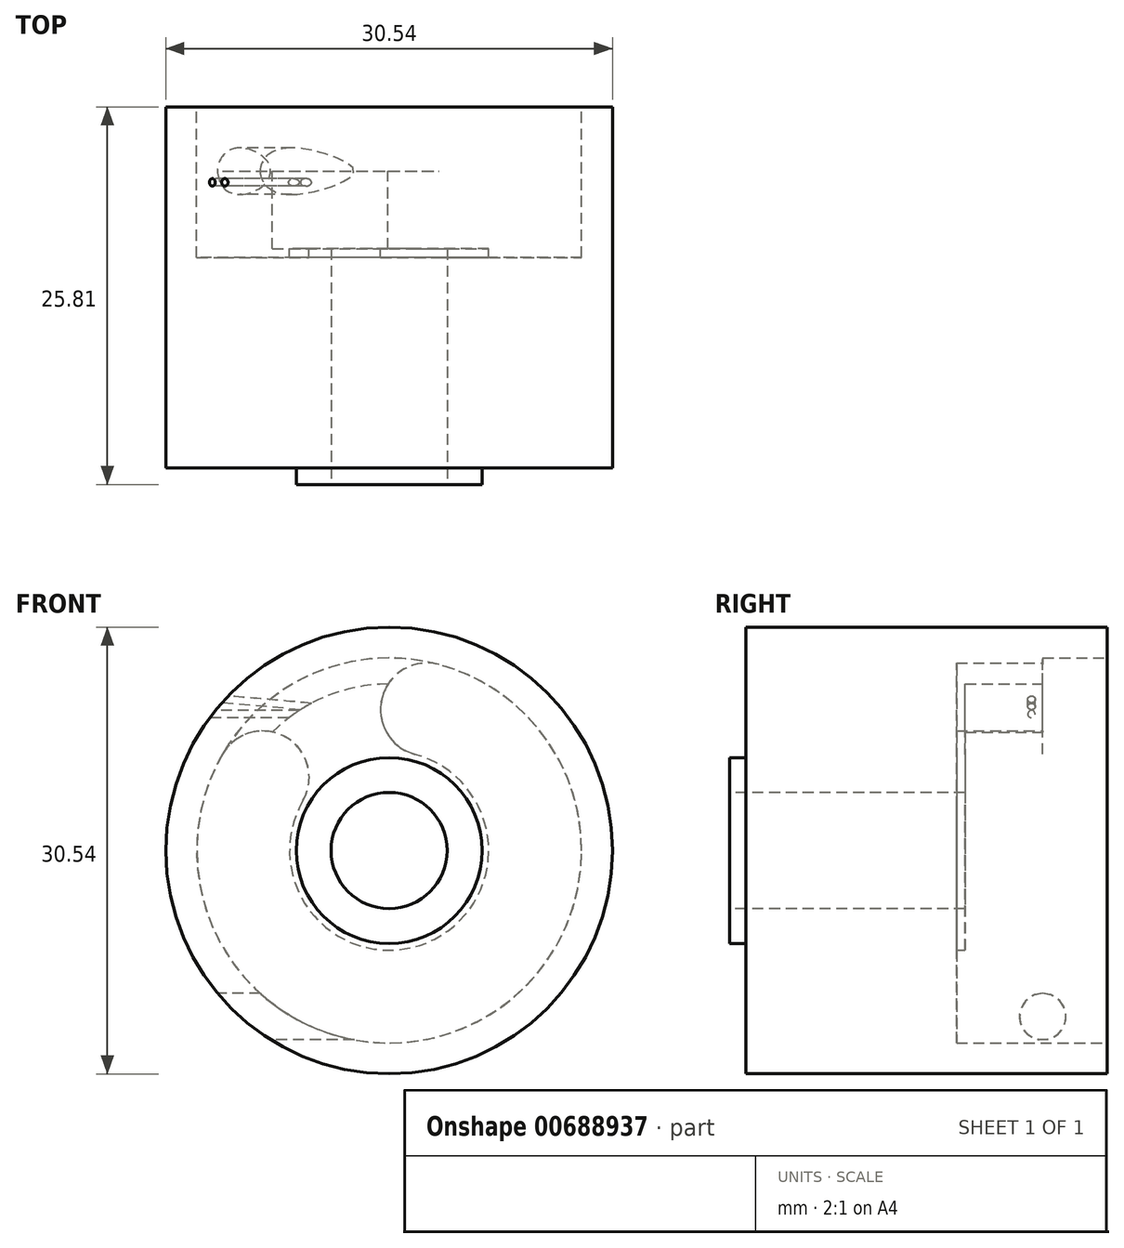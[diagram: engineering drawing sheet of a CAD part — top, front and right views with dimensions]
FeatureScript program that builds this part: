
annotation { "Feature Type Name" : "Feature", "Feature Type Description" : "" }
export const myFeature = defineFeature(function(context is Context, id is Id, definition is map)
    precondition{}
    {
        {
            var Q0;
            Q0=qCreatedBy(makeId("Front.planeOp"),FACE);
            var sketch = newSketch(context, id + "F0", { "sketchPlane" : qUnion([Q0])});
            skCircle(sketch, "E0", {"center": v(0, 0) * mm, "radius": 3.97 * mm});
            skCircle(sketch, "E1", {"center": v(0, 0) * mm, "radius": 15.27 * mm});
            skSolve(sketch);
        }
        {
            var Q0;
            Q0=qSketchRegion(id+"F0",true);
            extrude(context, id + "F1", {"entities" : qUnion([Q0]), "oppositeDirection" : true, "depth" : 24.7 * mm});
        }
        {
            var Q0;
            Q0=qCreatedBy(makeId("Front.planeOp"),FACE);
            var sketch = newSketch(context, id + "F2", { "sketchPlane" : qUnion([Q0])});
            skCircle(sketch, "E2", {"center": v(0, 0) * mm, "radius": 3.97 * mm});
            skCircle(sketch, "E3", {"center": v(0, 0) * mm, "radius": 6.35 * mm});
            skSolve(sketch);
        }
        {
            var Q0;
            Q0=qSketchRegion(id+"F2",true);
            extrude(context, id + "F3", {"entities" : qUnion([Q0]), "operationType" : NewBodyOperationType.ADD, "depth" : 1.12 * mm});
        }
        {
            var Q0;
            Q0=makeQuery(id+"F1.opExtrude","CAP_FACE",FACE,{"disambiguationData":[OSD([sQuery(id+"F0.wireOp",EDGE,"E0"),sQuery(id+"F0.wireOp",EDGE,"E1")])],"isStart":false});
            var sketch = newSketch(context, id + "F4", { "sketchPlane" : qUnion([Q0])});
            skCircle(sketch, "E4", {"center": v(0, 0) * mm, "radius": 13.16 * mm});
            skSolve(sketch);
        }
        {
            var Q0;
            Q0=qSketchRegion(id+"F4",true);
            extrude(context, id + "F5", {"entities" : qUnion([Q0]), "operationType" : NewBodyOperationType.REMOVE, "oppositeDirection" : true, "depth" : 4.4 * mm});
        }
        {
            var Q0;
            Q0=makeQuery(id+"F5.boolean.opBoolean","COPY",FACE,{"derivedFrom":makeQuery(id+"F5.opExtrude","CAP_FACE",FACE,{"disambiguationData":[OSD([sQuery(id+"F4.wireOp",EDGE,"E4")])],"isStart":false})});
            var sketch = newSketch(context, id + "F6", { "sketchPlane" : qUnion([Q0])});
            skCircle(sketch, "E5", {"center": v(0, 0) * mm, "radius": 9.98 * mm, "construction": true});
            skCircle(sketch, "E6", {"center": v(-2.58, 9.64) * mm, "radius": 3.18 * mm});
            skCircle(sketch, "E7", {"center": v(8.64, 5) * mm, "radius": 3.18 * mm});
            skArc(sketch, "E8", {"start": v(-3.4, 12.7) * mm, "mid": v(-5.04, -12.16) * mm, "end": v(11.4, 6.58) * mm});
            skArc(sketch, "E9", {"start": v(-1.76, 6.58) * mm, "mid": v(-2.6, -6.29) * mm, "end": v(5.9, 3.4) * mm});
            skLineSegment(sketch, "E10", {"start": v(0, 0) * mm, "end": v(0, 22.93) * mm, "construction": true});
            skLineSegment(sketch, "E11", {"start": v(0, 0) * mm, "end": v(-2.58, 9.64) * mm, "construction": true});
            skLineSegment(sketch, "E12", {"start": v(0, 0) * mm, "end": v(8.64, 5) * mm, "construction": true});
            skSolve(sketch);
        }
        {
            var Q0;
            Q0=qSketchRegion(id+"F6",true);
            extrude(context, id + "F7", {"entities" : qUnion([Q0]), "operationType" : NewBodyOperationType.REMOVE, "oppositeDirection" : true, "depth" : 5.9 * mm});
        }
        {
            var Q0;
            Q0=makeQuery(id+"F5.boolean.opBoolean","COPY",FACE,{"derivedFrom":makeQuery(id+"F5.opExtrude","CAP_FACE",FACE,{"disambiguationData":[OSD([sQuery(id+"F4.wireOp",EDGE,"E4")])],"isStart":false})});
            var sketch = newSketch(context, id + "F8", { "sketchPlane" : qUnion([Q0])});
            skCircle(sketch, "E13", {"center": v(0, 0) * mm, "radius": 11.38 * mm});
            skSolve(sketch);
        }
        {
            var Q0;
            Q0=qSketchRegion(id+"F8",true);
            extrude(context, id + "F9", {"entities" : qUnion([Q0]), "operationType" : NewBodyOperationType.REMOVE, "oppositeDirection" : true, "depth" : 5.3 * mm});
        }
        {
            var Q0;
            Q0=qCreatedBy(makeId("Right.planeOp"),FACE);
            cPlane(context, id + "F10", {"entities" : qUnion([Q0]), "cplaneType" : CPlaneType.OFFSET, "offset" : 15.27 * mm, "oppositeDirection" : true, "width" : 152.4 * mm, "height" : 152.4 * mm});
        }
        {
            var Q0;
            Q0=qCreatedBy(id+"F10.planeOp",FACE);
            var sketch = newSketch(context, id + "F11", { "sketchPlane" : qUnion([Q0])});
            skCircle(sketch, "E14", {"center": v(19.53, 10.87) * mm, "radius": 0.36 * mm, "construction": true});
            skCircle(sketch, "E15", {"center": v(20.3, -11.35) * mm, "radius": 1.59 * mm});
            skCircle(sketch, "E16", {"center": v(19.53, 9.32) * mm, "radius": 0.25 * mm});
            skSolve(sketch);
        }
        {
            var Q0;
            Q0=qSketchRegion(id+"F11",true);
            extrude(context, id + "F12", {"entities" : qUnion([Q0]), "operationType" : NewBodyOperationType.REMOVE, "depth" : 15.27 * mm, "offsetDistance" : 25.4 * mm});
        }
        {
            var Q0;
            Q0=makeQuery(id+"F1.opExtrude","CAP_FACE",FACE,{"disambiguationData":[OSD([sQuery(id+"F0.wireOp",EDGE,"E0"),sQuery(id+"F0.wireOp",EDGE,"E1")])],"isStart":false});
            var sketch = newSketch(context, id + "F13", { "sketchPlane" : qUnion([Q0])});
            skLineSegment(sketch, "E17", {"start": v(0, 0) * mm, "end": v(6.53, 9.32) * mm, "construction": true});
            skLineSegment(sketch, "E18", {"start": v(6.53, 9.32) * mm, "end": v(12.53, 5.12) * mm, "construction": true});
            skLineSegment(sketch, "E19", {"start": v(6.53, 9.32) * mm, "end": v(14.23, 9.32) * mm, "construction": true});
            skLineSegment(sketch, "E20", {"start": v(0, 0) * mm, "end": v(5.69, 9.85) * mm, "construction": true});
            skLineSegment(sketch, "E21", {"start": v(5.69, 9.85) * mm, "end": v(12.14, 10.42) * mm, "construction": true});
            skLineSegment(sketch, "E22", {"start": v(5.69, 9.85) * mm, "end": v(12.58, 5.88) * mm, "construction": true});
            skArc(sketch, "E23.0", {"start": v(8, 8.1) * mm, "mid": v(4.35, 10.51) * mm, "end": v(0.07, 11.38) * mm, "construction": true});
            skLineSegment(sketch, "E24", {"start": v(6.06, 9.63) * mm, "end": v(12.5, 10.2) * mm, "construction": true});
            skLineSegment(sketch, "E25", {"start": v(5.3, 10.07) * mm, "end": v(11.74, 10.64) * mm, "construction": true});
            skLineSegment(sketch, "E26", {"start": v(6.88, 9.07) * mm, "end": v(14.13, 9.07) * mm, "construction": true});
            skLineSegment(sketch, "E27", {"start": v(6.15, 9.58) * mm, "end": v(14.07, 9.58) * mm, "construction": true});
            skArc(sketch, "E28.0", {"start": v(12.28, 9.07) * mm, "mid": v(12.09, 9.32) * mm, "end": v(11.89, 9.58) * mm});
            skLineSegment(sketch, "E29", {"start": v(11.44, 10.1) * mm, "end": v(11.4, 10.6) * mm});
            skLineSegment(sketch, "E30", {"start": v(11.4, 10.6) * mm, "end": v(11, 10.58) * mm});
            skArc(sketch, "E31.trimOffspring", {"start": v(11.44, 10.1) * mm, "mid": v(11.23, 10.34) * mm, "end": v(11, 10.58) * mm});
            skSolve(sketch);
        }
        {
            var Q0;
            Q0 = qSketchRegion(id + "F13", true);
            extrude(context, id + "F14", {"entities" : qUnion([Q0]), "operationType" : NewBodyOperationType.ADD, "oppositeDirection" : true, "depth" : 12.7 * mm, "offsetDistance" : 25.4 * mm});
        }
        {
            var Q0;
            Q0=makeQuery(id+"F14.opExtrude","SWEPT_FACE",FACE,{"disambiguationData":[OSD([sQuery(id+"F13.wireOp",EDGE,"E29")])]});
            var sketch = newSketch(context, id + "F15", { "sketchPlane" : qUnion([Q0])});
            skCircle(sketch, "E32", {"center": v(-19.53, 9.31) * mm, "radius": 0.25 * mm});
            skSolve(sketch);
        }
        {
            var Q0;
            Q0 = qSketchRegion(id + "F15", true);
            extrude(context, id + "F16", {"entities" : qUnion([Q0]), "operationType" : NewBodyOperationType.REMOVE, "oppositeDirection" : true, "depth" : 12.7 * mm, "offsetDistance" : 25.4 * mm});
        }
        {
            var Q0;
            Q0=makeQuery(id+"F14.boolean.opBoolean","MERGE",FACE,{"derivedFrom":[makeQuery(id+"F1.opExtrude","CAP_FACE",FACE,{"disambiguationData":[OSD([sQuery(id+"F0.wireOp",EDGE,"E0"),sQuery(id+"F0.wireOp",EDGE,"E1")])],"isStart":false}),makeQuery(id+"F14.opExtrude","CAP_FACE",FACE,{"disambiguationData":[OSD([sQuery(id+"F13.wireOp",EDGE,"E29"),sQuery(id+"F13.wireOp",EDGE,"E30"),sQuery(id+"F13.wireOp",EDGE,"E31.trimOffspring")])],"isStart":true})]});
            var sketch = newSketch(context, id + "F17", { "sketchPlane" : qUnion([Q0])});
            skCircle(sketch, "E33", {"center": v(0, 0) * mm, "radius": 16.51 * mm});
            skCircle(sketch, "E34", {"center": v(0, 0) * mm, "radius": 15.27 * mm});
            skSolve(sketch);
        }
        {
            var Q0;
            Q0 = qSketchRegion(id + "F17", true);
            extrude(context, id + "F18", {"entities" : qUnion([Q0]), "operationType" : NewBodyOperationType.REMOVE, "oppositeDirection" : true, "depth" : 25.4 * mm, "offsetDistance" : 25.4 * mm});
        }
    });
